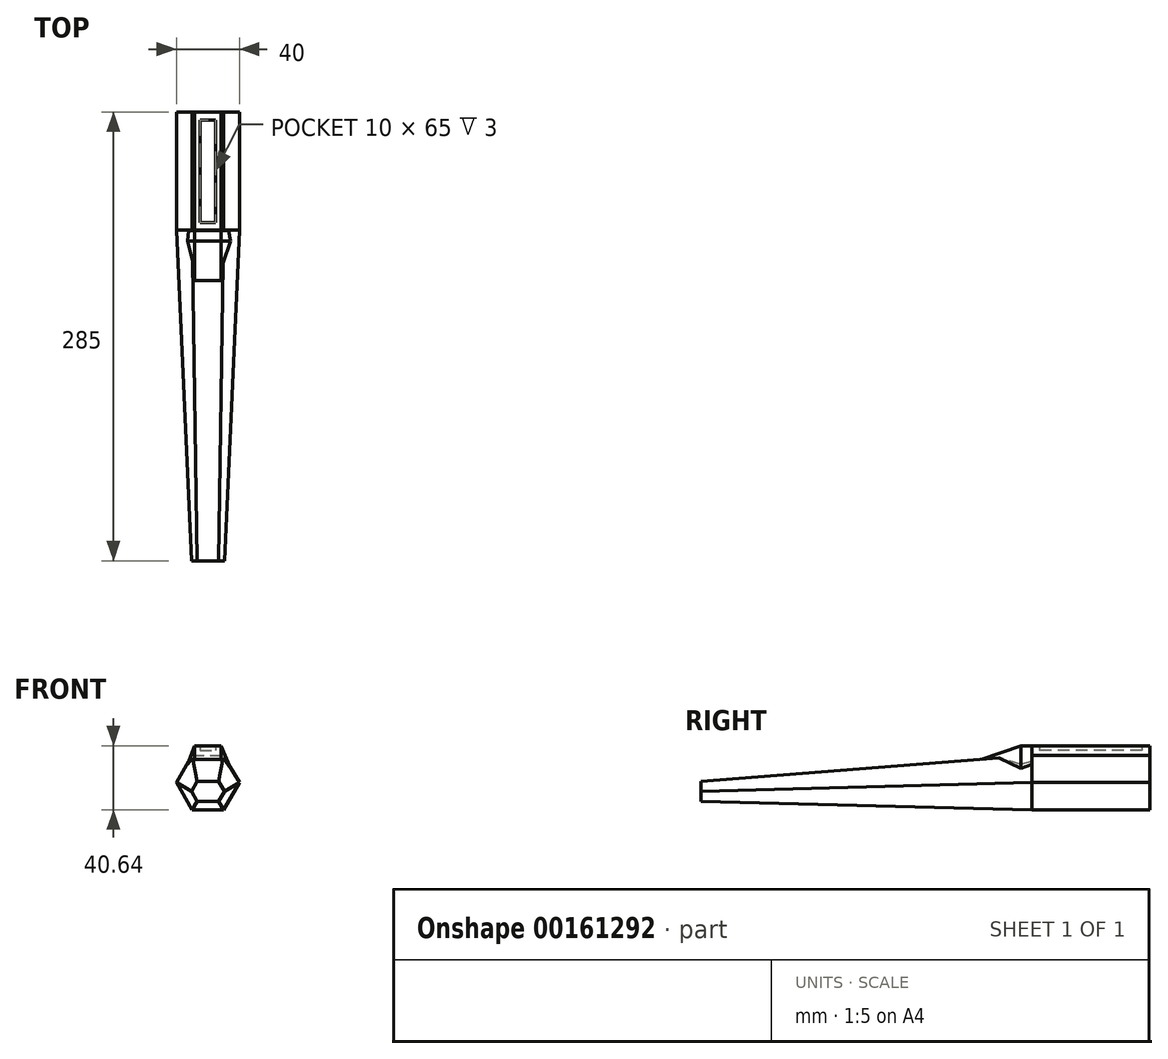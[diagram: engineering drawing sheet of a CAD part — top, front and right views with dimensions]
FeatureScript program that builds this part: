
annotation { "Feature Type Name" : "Feature", "Feature Type Description" : "" }
export const myFeature = defineFeature(function(context is Context, id is Id, definition is map)
    precondition{}
    {
        {
            var Q0;
            Q0=qCreatedBy(makeId("Front.planeOp"),FACE);
            var sketch = newSketch(context, id + "F0", { "sketchPlane" : qUnion([Q0])});
            skCircle(sketch, "E0.cCircle", {"center": v(0, 0) * mm, "radius": 20 * mm, "construction": true});
            skLineSegment(sketch, "E0.0", {"start": v(10, -17.32) * mm, "end": v(-10, -17.32) * mm});
            skLineSegment(sketch, "E0.1", {"start": v(-10, -17.32) * mm, "end": v(-20, 0) * mm});
            skLineSegment(sketch, "E0.2", {"start": v(-20, 0) * mm, "end": v(-10, 17.32) * mm});
            skLineSegment(sketch, "E0.3", {"start": v(-10, 17.32) * mm, "end": v(10, 17.32) * mm});
            skLineSegment(sketch, "E0.4", {"start": v(10, 17.32) * mm, "end": v(20, 0) * mm});
            skLineSegment(sketch, "E0.5", {"start": v(20, 0) * mm, "end": v(10, -17.32) * mm});
            skLineSegment(sketch, "E1", {"start": v(-10, 17.32) * mm, "end": v(-8.5, 23.32) * mm});
            skLineSegment(sketch, "E2", {"start": v(8.5, 23.32) * mm, "end": v(10, 17.32) * mm});
            skLineSegment(sketch, "E3", {"start": v(-8.5, 23.32) * mm, "end": v(8.5, 23.32) * mm});
            skLineSegment(sketch, "E4", {"start": v(0, 23.32) * mm, "end": v(0, 17.32) * mm, "construction": true});
            skSolve(sketch);
        }
        {
            var Q0;
            Q0=makeQuery(id+"F0.imprint","IMPRINT",FACE,{"disambiguationData":[TD([[makeQuery(id+"F0.imprint","IMPRINT",EDGE,{"derivedFrom":sQuery(id+"F0.wireOp",EDGE,"E0.0")}),-1.0]])]});
            extrude(context, id + "F1", {"entities" : qUnion([Q0]), "oppositeDirection" : true, "depth" : 75 * mm});
        }
        {
            var Q0;
            Q0=makeQuery(id+"F0.imprint","IMPRINT",FACE,{"disambiguationData":[TD([[makeQuery(id+"F0.imprint","IMPRINT",EDGE,{"derivedFrom":sQuery(id+"F0.wireOp",EDGE,"E0.0")}),-1.0]])]});
            var sketch = newSketch(context, id + "F2", { "sketchPlane" : qUnion([Q0])});
            skLineSegment(sketch, "E5.0", {"start": v(20, 0) * mm, "end": v(10, -17.32) * mm});
            skLineSegment(sketch, "E5.1", {"start": v(10, -17.32) * mm, "end": v(-10, -17.32) * mm});
            skLineSegment(sketch, "E5.2", {"start": v(-10, -17.32) * mm, "end": v(-20, 0) * mm});
            skPoint(sketch, "E5.0.midPoint", {"position": v(15, -8.66) * mm});
            skLineSegment(sketch, "E6", {"start": v(-20, 0) * mm, "end": v(20, 0) * mm});
            skSolve(sketch);
        }
        {
            var Q0;
            Q0=qSketchRegion(id+"F2",true);
            extrude(context, id + "F3", {"entities" : qUnion([Q0]), "operationType" : NewBodyOperationType.ADD, "depth" : 210 * mm, "hasDraft" : true, "draftAngle" : 1.5 * degree, "draftPullDirection" : true});
        }
        {
            var Q0;
            Q0=makeQuery(id+"F3.opExtrude","CAP_FACE",FACE,{"disambiguationData":[OSD([sQuery(id+"F2.wireOp",EDGE,"E5.0"),sQuery(id+"F2.wireOp",EDGE,"E5.1"),sQuery(id+"F2.wireOp",EDGE,"E5.2"),sQuery(id+"F2.wireOp",EDGE,"E6")])],"isStart":false});
            var sketch = newSketch(context, id + "F4", { "sketchPlane" : qUnion([Q0])});
            skLineSegment(sketch, "E7", {"start": v(10.48, -5.5) * mm, "end": v(-10.48, -5.5) * mm});
            skLineSegment(sketch, "E8", {"start": v(-10.48, -5.5) * mm, "end": v(-6.83, -11.82) * mm, "construction": true});
            skLineSegment(sketch, "E9", {"start": v(-6.83, -11.82) * mm, "end": v(6.83, -11.82) * mm, "construction": true});
            skLineSegment(sketch, "E10", {"start": v(6.83, -11.82) * mm, "end": v(10.48, -5.5) * mm, "construction": true});
            skLineSegment(sketch, "E11.MirrorCS", {"start": v(6.83, 0.82) * mm, "end": v(10.48, -5.5) * mm});
            skLineSegment(sketch, "E12.MirrorCS", {"start": v(-6.83, 0.82) * mm, "end": v(6.83, 0.82) * mm});
            skLineSegment(sketch, "E13.MirrorCS", {"start": v(-10.48, -5.5) * mm, "end": v(-6.83, 0.82) * mm});
            skSolve(sketch);
        }
        {
            var Q0;
            Q0=makeQuery(id+"F0.imprint","IMPRINT",FACE,{"disambiguationData":[TD([[makeQuery(id+"F0.imprint","IMPRINT",EDGE,{"derivedFrom":sQuery(id+"F0.wireOp",EDGE,"E0.0")}),-1.0]])]});
            var sketch = newSketch(context, id + "F5", { "sketchPlane" : qUnion([Q0])});
            skCircle(sketch, "E14.cCircle", {"center": v(0, 0) * mm, "radius": 17.32 * mm, "construction": true});
            skLineSegment(sketch, "E14.0", {"start": v(-20, 0) * mm, "end": v(-10, 17.32) * mm});
            skLineSegment(sketch, "E14.1", {"start": v(-10, 17.32) * mm, "end": v(10, 17.32) * mm});
            skLineSegment(sketch, "E14.2", {"start": v(10, 17.32) * mm, "end": v(20, 0) * mm});
            skLineSegment(sketch, "E14.3", {"start": v(20, 0) * mm, "end": v(10, -17.32) * mm, "construction": true});
            skLineSegment(sketch, "E14.4", {"start": v(10, -17.32) * mm, "end": v(-10, -17.32) * mm, "construction": true});
            skLineSegment(sketch, "E14.5", {"start": v(-10, -17.32) * mm, "end": v(-20, 0) * mm, "construction": true});
            skPoint(sketch, "E14.0.midPoint", {"position": v(-15, 8.66) * mm});
            skLineSegment(sketch, "E15", {"start": v(-20, 0) * mm, "end": v(20, 0) * mm});
            skSolve(sketch);
        }
        {
            var Q1;
            Q1=qSketchRegion(id+"F4",true);
            var Q2;
            Q2=qSketchRegion(id+"F5",true);
            loft(context, id + "F6", {"operationType" : NewBodyOperationType.ADD, "sheetProfilesArray" : [{ "sheetProfileEntities" : qUnion([Q1]) }, { "sheetProfileEntities" : qUnion([Q2]) }]});
        }
        {
            var Q0;
            Q0=makeQuery(id+"F0.imprint","IMPRINT",FACE,{"disambiguationData":[TD([[makeQuery(id+"F0.imprint","IMPRINT",EDGE,{"derivedFrom":sQuery(id+"F0.wireOp",EDGE,"UZhGPua9-qUty-b4Qy-S1j6-so2uiTIZxOn7.bottom")}),1.0]])]});
            var Q1;
            Q1=makeQuery(id+"F0.imprint","IMPRINT",FACE,{"disambiguationData":[TD([[makeQuery(id+"F0.imprint","IMPRINT",EDGE,{"derivedFrom":sQuery(id+"F0.wireOp",EDGE,"E0.3")}),1.0]])]});
            var Q2;
            Q2=makeQuery(id+"F1.opExtrude","CAP_FACE",FACE,{"disambiguationData":[OSD([sQuery(id+"F0.wireOp",EDGE,"E0.0"),sQuery(id+"F0.wireOp",EDGE,"E0.1"),sQuery(id+"F0.wireOp",EDGE,"E0.2"),sQuery(id+"F0.wireOp",EDGE,"E0.4"),sQuery(id+"F0.wireOp",EDGE,"E0.5"),sQuery(id+"F0.wireOp",EDGE,"UZhGPua9-qUty-b4Qy-S1j6-so2uiTIZxOn7.bottom")])],"isStart":false});
            extrude(context, id + "F7", {"entities" : qUnion([Q0, Q1]), "operationType" : NewBodyOperationType.ADD, "endBound" : BoundingType.UP_TO_SURFACE, "oppositeDirection" : true, "endBoundEntityFace" : qUnion([Q2]), "depth" : 25 * mm});
        }
        {
            var Q0;
            Q0=qCreatedBy(makeId("Front.planeOp"),FACE);
            cPlane(context, id + "F8", {"entities" : qUnion([Q0]), "cplaneType" : CPlaneType.OFFSET, "offset" : 7 * mm, "width" : 150 * mm, "height" : 150 * mm});
        }
        {
            var Q0;
            Q0=makeQuery(id+"F0.imprint","IMPRINT",FACE,{"disambiguationData":[TD([[makeQuery(id+"F0.imprint","IMPRINT",EDGE,{"derivedFrom":sQuery(id+"F0.wireOp",EDGE,"E0.3")}),1.0]])]});
            cPlane(context, id + "F9", {"entities" : qUnion([Q0]), "cplaneType" : CPlaneType.OFFSET, "offset" : 5 * mm, "oppositeDirection" : true, "width" : 150 * mm, "height" : 150 * mm});
        }
        {
            var Q0;
            Q0=qCreatedBy(id+"F9.planeOp",FACE);
            var sketch = newSketch(context, id + "F10", { "sketchPlane" : qUnion([Q0])});
            skLineSegment(sketch, "E16.bottom", {"start": v(-5, 23.32) * mm, "end": v(5, 23.32) * mm});
            skLineSegment(sketch, "E16.top", {"start": v(-5, 20.32) * mm, "end": v(5, 20.32) * mm});
            skLineSegment(sketch, "E16.left", {"start": v(-5, 23.32) * mm, "end": v(-5, 20.32) * mm});
            skLineSegment(sketch, "E16.right", {"start": v(5, 23.32) * mm, "end": v(5, 20.32) * mm});
            skPoint(sketch, "E17", {"position": v(0, 20.32) * mm});
            skSolve(sketch);
        }
        {
            var Q0;
            Q0=qSketchRegion(id+"F10",true);
            extrude(context, id + "F11", {"entities" : qUnion([Q0]), "operationType" : NewBodyOperationType.REMOVE, "oppositeDirection" : true, "depth" : 65 * mm});
        }
        {
            var Q0;
            Q0=qCreatedBy(id+"F8.planeOp",FACE);
            var sketch = newSketch(context, id + "F12", { "sketchPlane" : qUnion([Q0])});
            skLineSegment(sketch, "E18", {"start": v(-15.4, 4.96) * mm, "end": v(-8.5, 23.32) * mm});
            skLineSegment(sketch, "E19", {"start": v(-8.5, 23.32) * mm, "end": v(8.5, 23.32) * mm});
            skLineSegment(sketch, "E20", {"start": v(8.5, 23.32) * mm, "end": v(16.02, 4.96) * mm});
            skLineSegment(sketch, "E21", {"start": v(16.02, 4.96) * mm, "end": v(-15.4, 4.96) * mm});
            skSolve(sketch);
        }
        {
            var Q0;
            Q0=qCreatedBy(makeId("Right.planeOp"),FACE);
            var sketch = newSketch(context, id + "F13", { "sketchPlane" : qUnion([Q0])});
            skLineSegment(sketch, "E22", {"start": v(-7.15, 23.34) * mm, "end": v(-35.06, 13.8) * mm});
            skSolve(sketch);
        }
        {
            var Q0;
            Q0=makeQuery(id+"F12.imprint","IMPRINT",FACE,{"disambiguationData":[TD([[makeQuery(id+"F12.imprint","IMPRINT",EDGE,{"derivedFrom":sQuery(id+"F12.wireOp",EDGE,"E18")}),-1.0]])]});
            var Q1;
            Q1=sQuery(id+"F13.wireOp",EDGE,"E22");
            sweep(context, id + "F14", {"operationType" : NewBodyOperationType.ADD, "profiles" : qUnion([Q0]), "path" : qUnion([Q1])});
        }
        {
            var Q0;
            Q0=qCreatedBy(makeId("Right.planeOp"),FACE);
            var sketch = newSketch(context, id + "F15", { "sketchPlane" : qUnion([Q0])});
            skLineSegment(sketch, "E23", {"start": v(-6.95, 23.37) * mm, "end": v(0, 23.37) * mm});
            skSolve(sketch);
        }
        {
            var Q0;
            Q0=qSketchRegion(id+"F12",true);
            var Q1;
            Q1=qConstructionFilter(qBodyType(qCreatedBy(id+"F15",EDGE),BodyType.WIRE),ConstructionObject.NO);
            sweep(context, id + "F16", {"operationType" : NewBodyOperationType.ADD, "profiles" : qUnion([Q0]), "path" : qUnion([Q1])});
        }
    });
